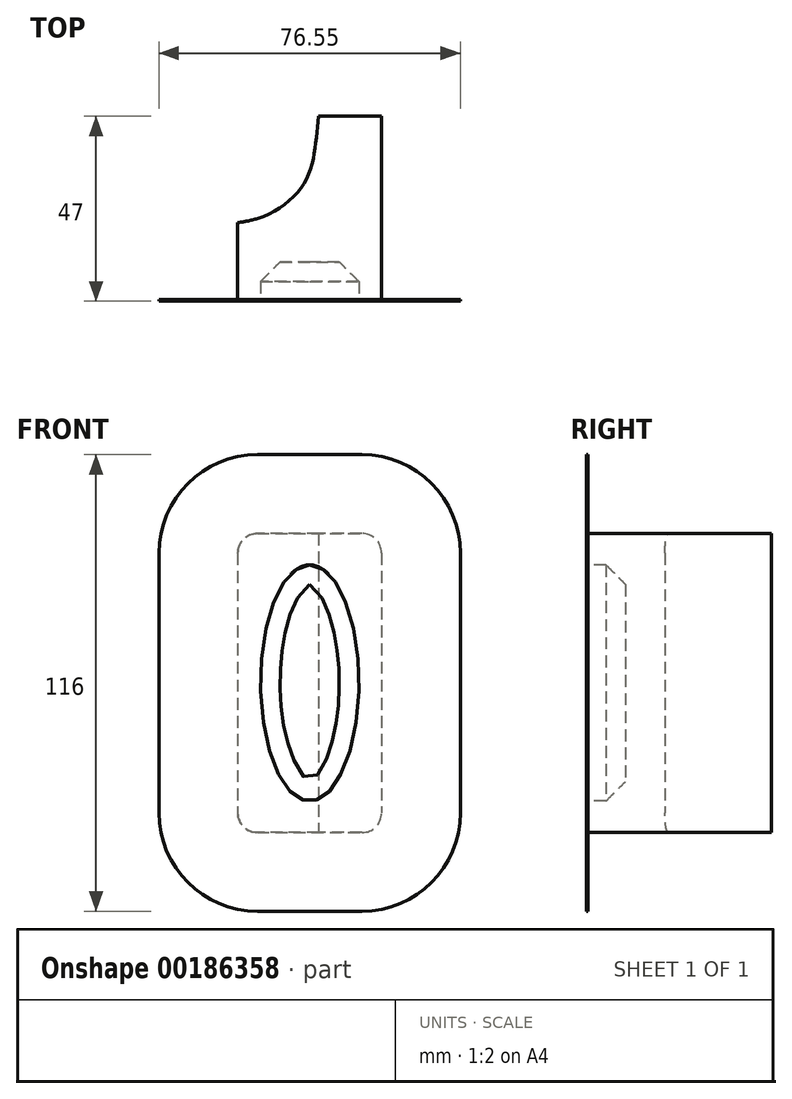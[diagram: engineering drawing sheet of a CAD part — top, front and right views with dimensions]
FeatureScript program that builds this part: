
annotation { "Feature Type Name" : "Feature", "Feature Type Description" : "" }
export const myFeature = defineFeature(function(context is Context, id is Id, definition is map)
    precondition{}
    {
        {
            var Q0;
            Q0=qCreatedBy(makeId("Top.planeOp"),FACE);
            var sketch = newSketch(context, id + "F0", { "sketchPlane" : qUnion([Q0])});
            skLineSegment(sketch, "E0", {"start": v(0, 0) * mm, "end": v(36.55, 0) * mm});
            skLineSegment(sketch, "E1", {"start": v(36.55, 0) * mm, "end": v(36.55, 47) * mm});
            skLineSegment(sketch, "E2", {"start": v(36.55, 47) * mm, "end": v(20.55, 47) * mm});
            skFitSpline(sketch, "E3", {"points": [v(20.55, 47) * mm, v(17.15, 30.5) * mm, v(0, 20) * mm], "startDerivative": vector(-4.97, -35.02) * mm, "endDerivative": vector(-43.61, -4.06) * mm});
            skLineSegment(sketch, "E4", {"start": v(0, 0) * mm, "end": v(0, 20) * mm});
            skSolve(sketch);
        }
        {
            var Q0;
            Q0=makeQuery(id+"F0.imprint","IMPRINT",FACE,{"disambiguationData":[TD([[makeQuery(id+"F0.imprint","IMPRINT",EDGE,{"derivedFrom":sQuery(id+"F0.wireOp",EDGE,"E0")}),1.0]])]});
            extrude(context, id + "F1", {"entities" : qUnion([Q0]), "depth" : 76 * mm});
        }
        {
            var Q0;
            Q0=makeQuery(id+"F1.opExtrude","CAP_EDGE",EDGE,{"disambiguationData":[OSD([sQuery(id+"F0.wireOp",EDGE,"E4")])],"isStart":false});
            var Q1;
            Q1=makeQuery(id+"F1.opExtrude","CAP_EDGE",EDGE,{"disambiguationData":[OSD([sQuery(id+"F0.wireOp",EDGE,"E1")])],"isStart":false});
            var Q2;
            Q2=makeQuery(id+"F1.opExtrude","CAP_EDGE",EDGE,{"disambiguationData":[OSD([sQuery(id+"F0.wireOp",EDGE,"E1")])],"isStart":true});
            var Q3;
            Q3=makeQuery(id+"F1.opExtrude","CAP_EDGE",EDGE,{"disambiguationData":[OSD([sQuery(id+"F0.wireOp",EDGE,"E4")])],"isStart":true});
            fillet(context, id + "F2", {"entities" : qUnion([Q0, Q1, Q2, Q3]), "radius" : 5 * mm, "tangentPropagation" : true, "allowEdgeOverflow" : false});
        }
        {
            var Q0;
            Q0=makeQuery(id+"F1.opExtrude","SWEPT_FACE",FACE,{"disambiguationData":[OSD([sQuery(id+"F0.wireOp",EDGE,"E0")])]});
            var sketch = newSketch(context, id + "F3", { "sketchPlane" : qUnion([Q0])});
            skLineSegment(sketch, "E5", {"start": v(0, 38) * mm, "end": v(36.55, 38) * mm, "construction": true});
            skEllipse(sketch, "E6", {"center": v(18.27, 38) * mm, "majorRadius": 30 * mm, "minorRadius": 12.5 * mm, "majorAxis": v(0, 1)});
            skSolve(sketch);
        }
        {
            var Q0;
            Q0 = qSketchRegion(id + "F3", true);
            extrude(context, id + "F4", {"entities" : qUnion([Q0]), "operationType" : NewBodyOperationType.REMOVE, "oppositeDirection" : true, "depth" : 10 * mm});
        }
        {
            var Q0;
            Q0=makeQuery(id+"F4.boolean.opBoolean","COPY",EDGE,{"derivedFrom":makeQuery(id+"F4.opExtrude","CAP_EDGE",EDGE,{"disambiguationData":[OSD([sQuery(id+"F3.wireOp",EDGE,"E6")])],"isStart":false})});
            chamfer(context, id + "F5", {"entities" : qUnion([Q0]), "width" : 5 * mm, "tangentPropagation" : true});
        }
        {
            var Q0;
            Q0=makeQuery(id+"F1.opExtrude","SWEPT_FACE",FACE,{"disambiguationData":[OSD([sQuery(id+"F0.wireOp",EDGE,"E0")])]});
            var sketch = newSketch(context, id + "F6", { "sketchPlane" : qUnion([Q0])});
            skArc(sketch, "E7.0", {"start": v(5, 96) * mm, "mid": v(-12.68, 88.68) * mm, "end": v(-20, 71) * mm});
            skLineSegment(sketch, "E7.1", {"start": v(-20, 71) * mm, "end": v(-20, 5) * mm});
            skLineSegment(sketch, "E7.2", {"start": v(5, 96) * mm, "end": v(31.55, 96) * mm});
            skArc(sketch, "E7.3", {"start": v(-20, 5) * mm, "mid": v(-12.68, -12.68) * mm, "end": v(5, -20) * mm});
            skArc(sketch, "E7.4", {"start": v(56.55, 71) * mm, "mid": v(49.23, 88.68) * mm, "end": v(31.55, 96) * mm});
            skLineSegment(sketch, "E7.5", {"start": v(56.55, 71) * mm, "end": v(56.55, 5) * mm});
            skArc(sketch, "E7.6", {"start": v(31.55, -20) * mm, "mid": v(49.23, -12.68) * mm, "end": v(56.55, 5) * mm});
            skLineSegment(sketch, "E7.7", {"start": v(5, -20) * mm, "end": v(31.55, -20) * mm});
            skSolve(sketch);
        }
        {
            var Q0;
            Q0=makeQuery(id+"F6.imprint","IMPRINT",FACE,{"disambiguationData":[TD([[makeQuery(id+"F6.imprint","IMPRINT",EDGE,{"derivedFrom":sQuery(id+"F6.wireOp",EDGE,"E7.0")}),1.0]])]});
            extrude(context, id + "F7", {"entities" : qUnion([Q0]), "operationType" : NewBodyOperationType.ADD, "oppositeDirection" : true, "depth" : .4 * mm});
        }
    });
